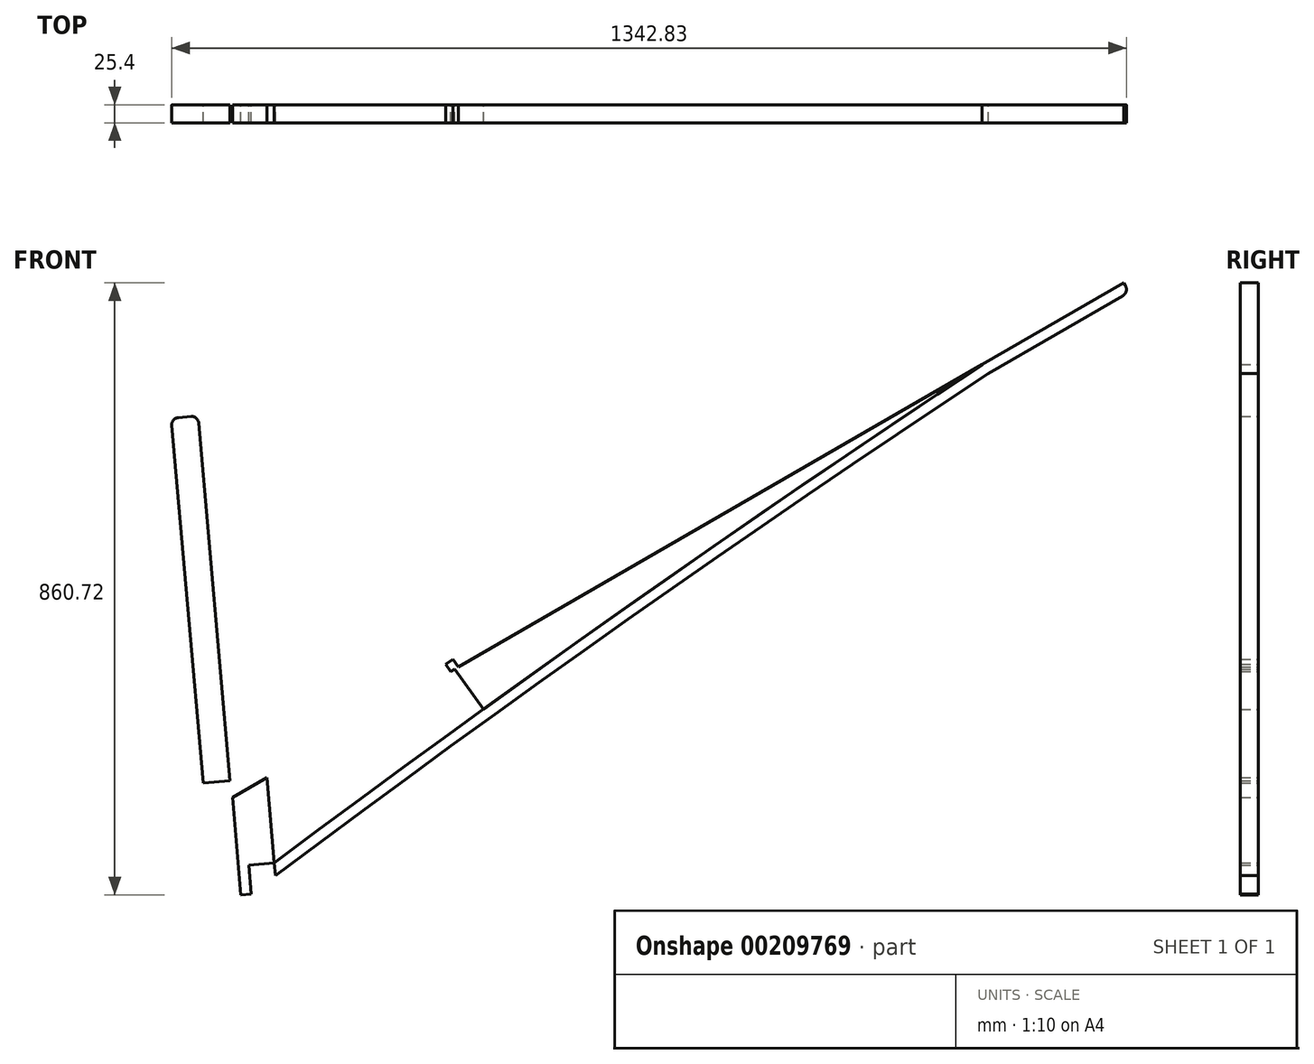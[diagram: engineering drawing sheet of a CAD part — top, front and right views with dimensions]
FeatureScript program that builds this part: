
annotation { "Feature Type Name" : "Feature", "Feature Type Description" : "" }
export const myFeature = defineFeature(function(context is Context, id is Id, definition is map)
    precondition{}
    {
        {
            var Q0;
            Q0=qCreatedBy(makeId("Front.planeOp"),FACE);
            var sketch = newSketch(context, id + "F0", { "sketchPlane" : qUnion([Q0])});
            skLineSegment(sketch, "E0", {"start": v(0.89, -10.12) * mm, "end": v(177.1, -2024.27) * mm});
            skLineSegment(sketch, "E1", {"start": v(0, 0) * mm, "end": v(2540, 0) * mm, "construction": true});
            skLineSegment(sketch, "E2", {"start": v(-279.2, -744.3) * mm, "end": v(1339.78, 190.41) * mm});
            skLineSegment(sketch, "E3", {"start": v(0, 0) * mm, "end": v(0, -2540) * mm, "construction": true});
            skLineSegment(sketch, "E4", {"start": v(62.95, -2024.27) * mm, "end": v(824.95, -2024.27) * mm});
            skLineSegment(sketch, "E5.0", {"start": v(38.84, -6.8) * mm, "end": v(215.35, -2024.27) * mm});
            skLineSegment(sketch, "E6", {"start": v(27.83, 2.44) * mm, "end": v(10.12, 0.89) * mm});
            skLineSegment(sketch, "E7", {"start": v(215.35, -2024.27) * mm, "end": v(177.1, -2024.27) * mm});
            skLineSegment(sketch, "E8.0", {"start": v(-298.26, -711.31) * mm, "end": v(1311.93, 218.33) * mm});
            skLineSegment(sketch, "E9", {"start": v(-293.08, -740.59) * mm, "end": v(-301.97, -725.2) * mm});
            skLineSegment(sketch, "E10", {"start": v(1339.78, 190.41) * mm, "end": v(1325.8, 214.6) * mm});
            skPoint(sketch, "E11", {"position": v(44.9, -513.2) * mm});
            skLineSegment(sketch, "E12", {"start": v(44.9, -513.2) * mm, "end": v(134.7, -505.33) * mm});
            skLineSegment(sketch, "E13", {"start": v(134.7, -505.33) * mm, "end": v(147.87, -655.76) * mm});
            skLineSegment(sketch, "E14", {"start": v(138.63, -666.77) * mm, "end": v(58.94, -673.74) * mm});
            skLineSegment(sketch, "E15", {"start": v(58.94, -673.74) * mm, "end": v(44.9, -513.2) * mm});
            skLineSegment(sketch, "E16", {"start": v(44.9, -513.2) * mm, "end": v(26.93, -514.76) * mm});
            skLineSegment(sketch, "E17", {"start": v(26.93, -514.76) * mm, "end": v(40.1, -665.2) * mm});
            skLineSegment(sketch, "E18", {"start": v(51.1, -674.43) * mm, "end": v(58.94, -673.74) * mm});
            skPoint(sketch, "E19", {"position": v(84.97, -534.05) * mm});
            skPoint(sketch, "E20", {"position": v(1140.83, 75.55) * mm});
            skLineSegment(sketch, "E21", {"start": v(147.18, -647.92) * mm, "end": v(39.4, -657.35) * mm, "construction": true});
            skCircle(sketch, "E22", {"center": v(129.22, -649.49) * mm, "radius": 8.26 * mm});
            skLineSegment(sketch, "E23", {"start": v(134.7, -505.33) * mm, "end": v(131.04, -463.46) * mm});
            skLineSegment(sketch, "E24", {"start": v(131.04, -463.46) * mm, "end": v(23.27, -472.89) * mm});
            skLineSegment(sketch, "E25", {"start": v(23.27, -472.89) * mm, "end": v(26.93, -514.76) * mm});
            skPoint(sketch, "E26", {"position": v(398.67, -352.93) * mm});
            skLineSegment(sketch, "E27", {"start": v(398.67, -352.93) * mm, "end": v(433.6, -413.43) * mm, "construction": true});
            skPoint(sketch, "E28", {"position": v(145.22, -625.53) * mm});
            skArc(sketch, "E29", {"start": v(1140.83, 75.55) * mm, "mid": v(637.9, -267.71) * mm, "end": v(145.22, -625.53) * mm});
            skArc(sketch, "E30.0", {"start": v(1149.23, 62.84) * mm, "mid": v(642.8, -282.9) * mm, "end": v(146.79, -643.4) * mm});
            skLineSegment(sketch, "E31", {"start": v(398.67, -352.93) * mm, "end": v(439.34, -409.28) * mm});
            skLineSegment(sketch, "E32.0", {"start": v(394.17, -357.54) * mm, "end": v(434.2, -413) * mm});
            skLineSegment(sketch, "E33.0", {"start": v(403.82, -349.22) * mm, "end": v(444.5, -405.56) * mm});
            skLineSegment(sketch, "E34", {"start": v(1339.78, 190.41) * mm, "end": v(1342.32, 186.01) * mm});
            skLineSegment(sketch, "E35", {"start": v(1149.23, 62.84) * mm, "end": v(1338.6, 172.13) * mm});
            skLineSegment(sketch, "E36.0", {"start": v(39.22, 3.43) * mm, "end": v(216.32, -2020.84) * mm, "construction": true});
            skLineSegment(sketch, "E37.0", {"start": v(-1.27, -0.11) * mm, "end": v(175.84, -2024.38) * mm, "construction": true});
            skLineSegment(sketch, "E38", {"start": v(39.97, -471.42) * mm, "end": v(57.67, -673.74) * mm});
            skLineSegment(sketch, "E39", {"start": v(80.45, -467.88) * mm, "end": v(98.16, -670.3) * mm});
            skLineSegment(sketch, "E40", {"start": v(145.22, -625.53) * mm, "end": v(109.3, -628.67) * mm});
            skLineSegment(sketch, "E41", {"start": v(109.3, -628.67) * mm, "end": v(112.82, -669.03) * mm});
            skPoint(sketch, "E42.visualSharp", {"position": v(148.75, -665.88) * mm});
            skArc(sketch, "E42.filletArc", {"start": v(138.63, -666.77) * mm, "mid": v(145.53, -663.18) * mm, "end": v(147.87, -655.76) * mm});
            skLineSegment(sketch, "E43", {"start": v(403.82, -349.22) * mm, "end": v(396.39, -338.92) * mm});
            skLineSegment(sketch, "E44", {"start": v(396.39, -338.92) * mm, "end": v(386.1, -346.35) * mm});
            skLineSegment(sketch, "E45", {"start": v(386.1, -346.35) * mm, "end": v(394.17, -357.54) * mm});
            skLineSegment(sketch, "E46", {"start": v(1140.83, 75.55) * mm, "end": v(1134.42, 86.65) * mm});
            skLineSegment(sketch, "E47", {"start": v(1134.42, 86.65) * mm, "end": v(1148.16, 94.59) * mm});
            skLineSegment(sketch, "E48", {"start": v(1148.16, 94.59) * mm, "end": v(1154.58, 83.49) * mm});
            skLineSegment(sketch, "E49", {"start": v(1326.03, 182.47) * mm, "end": v(1319.68, 193.47) * mm});
            skLineSegment(sketch, "E50", {"start": v(1319.68, 193.47) * mm, "end": v(1333.43, 201.41) * mm});
            skPoint(sketch, "E51.visualSharp", {"position": v(1347.4, 177.21) * mm});
            skArc(sketch, "E51.filletArc", {"start": v(1338.6, 172.13) * mm, "mid": v(1343.33, 178.3) * mm, "end": v(1342.32, 186.01) * mm});
            skPoint(sketch, "E52.visualSharp", {"position": v(1320.73, 223.4) * mm});
            skArc(sketch, "E52.filletArc", {"start": v(1325.8, 214.6) * mm, "mid": v(1319.64, 219.34) * mm, "end": v(1311.93, 218.33) * mm});
            skLineSegment(sketch, "E53.0", {"start": v(6.19, -484.58) * mm, "end": v(8.97, -516.34) * mm});
            skLineSegment(sketch, "E54", {"start": v(23.27, -472.89) * mm, "end": v(15.43, -473.57) * mm});
            skLineSegment(sketch, "E55", {"start": v(8.97, -516.34) * mm, "end": v(10.43, -533.1) * mm});
            skCircle(sketch, "E56", {"center": v(25.1, -491.17) * mm, "radius": 8.26 * mm});
            skPoint(sketch, "E57.visualSharp", {"position": v(5.3, -474.46) * mm});
            skArc(sketch, "E57.filletArc", {"start": v(15.43, -473.57) * mm, "mid": v(8.53, -477.16) * mm, "end": v(6.19, -484.58) * mm});
            skPoint(sketch, "E58.visualSharp", {"position": v(40.98, -675.31) * mm});
            skArc(sketch, "E58.filletArc", {"start": v(40.1, -665.2) * mm, "mid": v(43.68, -672.09) * mm, "end": v(51.1, -674.43) * mm});
            skPoint(sketch, "E59.visualSharp", {"position": v(37.96, 3.32) * mm});
            skArc(sketch, "E59.filletArc", {"start": v(38.84, -6.8) * mm, "mid": v(35.25, 0.1) * mm, "end": v(27.83, 2.44) * mm});
            skPoint(sketch, "E60.visualSharp", {"position": v(0, 0) * mm});
            skArc(sketch, "E60.filletArc", {"start": v(10.12, 0.89) * mm, "mid": v(3.22, -2.7) * mm, "end": v(0.89, -10.12) * mm});
            skPoint(sketch, "E61.visualSharp", {"position": v(-307.05, -716.4) * mm});
            skArc(sketch, "E61.filletArc", {"start": v(-298.26, -711.31) * mm, "mid": v(-302.99, -717.48) * mm, "end": v(-301.97, -725.2) * mm});
            skPoint(sketch, "E62.visualSharp", {"position": v(-288, -749.39) * mm});
            skArc(sketch, "E62.filletArc", {"start": v(-293.08, -740.59) * mm, "mid": v(-286.92, -745.32) * mm, "end": v(-279.2, -744.3) * mm});
            skLineSegment(sketch, "E63", {"start": v(147.12, -1771.92) * mm, "end": v(233.4, -1764.37) * mm});
            skLineSegment(sketch, "E64", {"start": v(244.41, -1773.6) * mm, "end": v(266.34, -2024.27) * mm});
            skLineSegment(sketch, "E65", {"start": v(137.88, -1782.93) * mm, "end": v(159, -2024.27) * mm});
            skPoint(sketch, "E66", {"position": v(192.92, -1767.91) * mm});
            skPoint(sketch, "E67", {"position": v(154.96, -1771.23) * mm});
            skLineSegment(sketch, "E68.0", {"start": v(62.95, -2042.3) * mm, "end": v(824.95, -2042.3) * mm});
            skLineSegment(sketch, "E69.0", {"start": v(73.1, -1988.2) * mm, "end": v(824.95, -1988.2) * mm});
            skLineSegment(sketch, "E70", {"start": v(62.95, -1998.36) * mm, "end": v(62.95, -2024.27) * mm});
            skLineSegment(sketch, "E71", {"start": v(62.95, -2042.3) * mm, "end": v(62.95, -2024.27) * mm});
            skLineSegment(sketch, "E72", {"start": v(824.95, -1988.2) * mm, "end": v(824.95, -2024.27) * mm});
            skLineSegment(sketch, "E73", {"start": v(824.95, -2024.27) * mm, "end": v(824.95, -2042.3) * mm});
            skLineSegment(sketch, "E74", {"start": v(774.15, -2024.27) * mm, "end": v(774.15, -2042.3) * mm});
            skLineSegment(sketch, "E75.bottom", {"start": v(266.34, -2024.27) * mm, "end": v(317.14, -2024.27) * mm});
            skLineSegment(sketch, "E75.top", {"start": v(266.34, -2042.3) * mm, "end": v(317.14, -2042.3) * mm});
            skLineSegment(sketch, "E75.left", {"start": v(266.34, -2024.27) * mm, "end": v(266.34, -2042.3) * mm});
            skLineSegment(sketch, "E75.right", {"start": v(317.14, -2024.27) * mm, "end": v(317.14, -2042.3) * mm});
            skLineSegment(sketch, "E76.bottom", {"start": v(62.95, -2024.27) * mm, "end": v(113.75, -2024.27) * mm});
            skLineSegment(sketch, "E76.top", {"start": v(62.95, -2042.3) * mm, "end": v(113.75, -2042.3) * mm});
            skLineSegment(sketch, "E76.left", {"start": v(62.95, -2024.27) * mm, "end": v(62.95, -2042.3) * mm});
            skLineSegment(sketch, "E76.right", {"start": v(113.75, -2024.27) * mm, "end": v(113.75, -2042.3) * mm});
            skPoint(sketch, "E77.visualSharp", {"position": v(62.95, -1988.2) * mm});
            skArc(sketch, "E77.filletArc", {"start": v(73.1, -1988.2) * mm, "mid": v(65.92, -1991.18) * mm, "end": v(62.95, -1998.36) * mm});
            skPoint(sketch, "E78.visualSharp", {"position": v(243.52, -1763.49) * mm});
            skArc(sketch, "E78.filletArc", {"start": v(244.41, -1773.6) * mm, "mid": v(240.82, -1766.7) * mm, "end": v(233.4, -1764.37) * mm});
            skPoint(sketch, "E79.visualSharp", {"position": v(137, -1772.8) * mm});
            skArc(sketch, "E79.filletArc", {"start": v(147.12, -1771.92) * mm, "mid": v(140.22, -1775.51) * mm, "end": v(137.88, -1782.93) * mm});
            skPoint(sketch, "E80", {"position": v(155.84, -1988.2) * mm});
            skLineSegment(sketch, "E81", {"start": v(155.84, -1988.2) * mm, "end": v(159, -2024.27) * mm});
            skCircle(sketch, "E82", {"center": v(157.42, -2006.23) * mm, "radius": 8.26 * mm});
            skLineSegment(sketch, "E83", {"start": v(195.78, -1786.02) * mm, "end": v(245.12, -1781.7) * mm, "construction": true});
            skCircle(sketch, "E84", {"center": v(220.45, -1783.86) * mm, "radius": 8.26 * mm});
            skPoint(sketch, "E84.perimeterSnap0", {"position": v(220.45, -1783.86) * mm});
            skPoint(sketch, "E84.perimeterSnap1", {"position": v(190.26, -1768.15) * mm});
            skLineSegment(sketch, "E85.bottom", {"start": v(73.1, -2194.7) * mm, "end": v(814.79, -2194.7) * mm});
            skLineSegment(sketch, "E85.top", {"start": v(73.1, -2499.5) * mm, "end": v(814.79, -2499.5) * mm});
            skLineSegment(sketch, "E85.left", {"start": v(62.95, -2204.86) * mm, "end": v(62.95, -2489.34) * mm});
            skLineSegment(sketch, "E85.right", {"start": v(824.95, -2204.86) * mm, "end": v(824.95, -2489.34) * mm});
            skLineSegment(sketch, "E86", {"start": v(62.95, -2347.1) * mm, "end": v(824.95, -2347.1) * mm, "construction": true});
            skLineSegment(sketch, "E87.0", {"start": v(62.95, -2365.14) * mm, "end": v(824.95, -2365.14) * mm, "construction": true});
            skLineSegment(sketch, "E88.0", {"start": v(62.95, -2329.07) * mm, "end": v(824.95, -2329.07) * mm, "construction": true});
            skLineSegment(sketch, "E89.bottom", {"start": v(266.34, -2329.07) * mm, "end": v(317.14, -2329.07) * mm});
            skLineSegment(sketch, "E89.top", {"start": v(266.34, -2311.03) * mm, "end": v(317.14, -2311.03) * mm});
            skLineSegment(sketch, "E89.left", {"start": v(266.34, -2329.07) * mm, "end": v(266.34, -2311.03) * mm});
            skLineSegment(sketch, "E89.right", {"start": v(317.14, -2329.07) * mm, "end": v(317.14, -2311.03) * mm});
            skLineSegment(sketch, "E90.bottom", {"start": v(774.15, -2329.07) * mm, "end": v(824.95, -2329.07) * mm});
            skLineSegment(sketch, "E90.top", {"start": v(774.15, -2311.03) * mm, "end": v(824.95, -2311.03) * mm});
            skLineSegment(sketch, "E90.left", {"start": v(774.15, -2329.07) * mm, "end": v(774.15, -2311.03) * mm});
            skLineSegment(sketch, "E90.right", {"start": v(824.95, -2329.07) * mm, "end": v(824.95, -2311.03) * mm});
            skLineSegment(sketch, "E91.bottom", {"start": v(62.95, -2311.03) * mm, "end": v(113.75, -2311.03) * mm});
            skLineSegment(sketch, "E91.top", {"start": v(62.95, -2329.07) * mm, "end": v(113.75, -2329.07) * mm});
            skLineSegment(sketch, "E91.left", {"start": v(62.95, -2311.03) * mm, "end": v(62.95, -2329.07) * mm});
            skLineSegment(sketch, "E91.right", {"start": v(113.75, -2311.03) * mm, "end": v(113.75, -2329.07) * mm});
            skLineSegment(sketch, "E92.MirrorCS", {"start": v(62.95, -2365.14) * mm, "end": v(113.75, -2365.14) * mm});
            skLineSegment(sketch, "E93.MirrorCS", {"start": v(266.34, -2365.14) * mm, "end": v(317.14, -2365.14) * mm});
            skLineSegment(sketch, "E94.MirrorCS", {"start": v(774.15, -2365.14) * mm, "end": v(824.95, -2365.14) * mm});
            skLineSegment(sketch, "E95.MirrorCS", {"start": v(62.95, -2383.17) * mm, "end": v(113.75, -2383.17) * mm});
            skLineSegment(sketch, "E96.MirrorCS", {"start": v(824.95, -2365.14) * mm, "end": v(824.95, -2383.17) * mm});
            skLineSegment(sketch, "E97.MirrorCS", {"start": v(266.34, -2383.17) * mm, "end": v(317.14, -2383.17) * mm});
            skLineSegment(sketch, "E98.MirrorCS", {"start": v(774.15, -2365.14) * mm, "end": v(774.15, -2383.17) * mm});
            skLineSegment(sketch, "E99.MirrorCS", {"start": v(317.14, -2365.14) * mm, "end": v(317.14, -2383.17) * mm});
            skLineSegment(sketch, "E100.MirrorCS", {"start": v(266.34, -2365.14) * mm, "end": v(266.34, -2383.17) * mm});
            skLineSegment(sketch, "E101.MirrorCS", {"start": v(62.95, -2383.17) * mm, "end": v(62.95, -2365.14) * mm});
            skLineSegment(sketch, "E102.MirrorCS", {"start": v(113.75, -2383.17) * mm, "end": v(113.75, -2365.14) * mm});
            skLineSegment(sketch, "E103.MirrorCS", {"start": v(774.15, -2383.17) * mm, "end": v(824.95, -2383.17) * mm});
            skPoint(sketch, "E104.visualSharp", {"position": v(62.95, -2194.7) * mm});
            skArc(sketch, "E104.filletArc", {"start": v(73.1, -2194.7) * mm, "mid": v(65.92, -2197.68) * mm, "end": v(62.95, -2204.86) * mm});
            skPoint(sketch, "E105.visualSharp", {"position": v(824.95, -2194.7) * mm});
            skArc(sketch, "E105.filletArc", {"start": v(824.95, -2204.86) * mm, "mid": v(821.97, -2197.68) * mm, "end": v(814.79, -2194.7) * mm});
            skPoint(sketch, "E106.visualSharp", {"position": v(824.95, -2499.5) * mm});
            skArc(sketch, "E106.filletArc", {"start": v(814.79, -2499.5) * mm, "mid": v(821.97, -2496.53) * mm, "end": v(824.95, -2489.34) * mm});
            skPoint(sketch, "E107.visualSharp", {"position": v(62.95, -2499.5) * mm});
            skArc(sketch, "E107.filletArc", {"start": v(62.95, -2489.34) * mm, "mid": v(65.92, -2496.53) * mm, "end": v(73.1, -2499.5) * mm});
            skPoint(sketch, "E108", {"position": v(81.3, -492.17) * mm});
            skLineSegment(sketch, "E109", {"start": v(131.04, -463.46) * mm, "end": v(84.97, -534.05) * mm, "construction": true});
            skLineSegment(sketch, "E110", {"start": v(81.3, -492.17) * mm, "end": v(134.7, -505.33) * mm, "construction": true});
            skCircle(sketch, "E111", {"center": v(108, -498.75) * mm, "radius": 8.26 * mm});
            skLineSegment(sketch, "E112", {"start": v(1267.05, 192.42) * mm, "end": v(1273.4, 181.42) * mm});
            skLineSegment(sketch, "E113", {"start": v(1273.4, 181.42) * mm, "end": v(1283.08, 187) * mm});
            skLineSegment(sketch, "E114", {"start": v(1283.08, 187) * mm, "end": v(1276.73, 198) * mm});
            skCircle(sketch, "E115", {"center": v(1271.18, 185.27) * mm, "radius": 4.45 * mm});
            skLineSegment(sketch, "E116", {"start": v(1169.39, 136.03) * mm, "end": v(1175.74, 125.03) * mm});
            skLineSegment(sketch, "E117", {"start": v(1175.74, 125.03) * mm, "end": v(1185.42, 130.62) * mm});
            skLineSegment(sketch, "E118", {"start": v(1185.42, 130.62) * mm, "end": v(1179.07, 141.62) * mm});
            skCircle(sketch, "E119", {"center": v(1173.51, 128.88) * mm, "radius": 4.45 * mm});
            skLineSegment(sketch, "E120", {"start": v(1179.07, 141.62) * mm, "end": v(1169.39, 136.03) * mm});
            skLineSegment(sketch, "E121", {"start": v(1071.72, 79.64) * mm, "end": v(1078.07, 68.65) * mm});
            skLineSegment(sketch, "E122", {"start": v(1078.07, 68.65) * mm, "end": v(1087.75, 74.23) * mm});
            skLineSegment(sketch, "E123", {"start": v(1087.75, 74.23) * mm, "end": v(1081.4, 85.23) * mm});
            skCircle(sketch, "E124", {"center": v(1075.85, 72.5) * mm, "radius": 4.45 * mm});
            skLineSegment(sketch, "E125", {"start": v(1081.4, 85.23) * mm, "end": v(1071.72, 79.64) * mm});
            skLineSegment(sketch, "E126", {"start": v(974.05, 23.26) * mm, "end": v(980.4, 12.26) * mm});
            skLineSegment(sketch, "E127", {"start": v(980.4, 12.26) * mm, "end": v(990.08, 17.85) * mm});
            skLineSegment(sketch, "E128", {"start": v(990.08, 17.85) * mm, "end": v(983.73, 28.84) * mm});
            skCircle(sketch, "E129", {"center": v(978.18, 16.1) * mm, "radius": 4.45 * mm});
            skLineSegment(sketch, "E130", {"start": v(983.73, 28.84) * mm, "end": v(974.05, 23.26) * mm});
            skLineSegment(sketch, "E131", {"start": v(876.39, -33.13) * mm, "end": v(882.74, -44.13) * mm});
            skLineSegment(sketch, "E132", {"start": v(882.74, -44.13) * mm, "end": v(892.42, -38.54) * mm});
            skLineSegment(sketch, "E133", {"start": v(892.42, -38.54) * mm, "end": v(886.07, -27.54) * mm});
            skCircle(sketch, "E134", {"center": v(880.51, -40.28) * mm, "radius": 4.45 * mm});
            skLineSegment(sketch, "E135", {"start": v(886.07, -27.54) * mm, "end": v(876.39, -33.13) * mm});
            skLineSegment(sketch, "E136", {"start": v(778.72, -89.52) * mm, "end": v(785.07, -100.52) * mm});
            skLineSegment(sketch, "E137", {"start": v(785.07, -100.52) * mm, "end": v(794.75, -94.93) * mm});
            skLineSegment(sketch, "E138", {"start": v(794.75, -94.93) * mm, "end": v(788.4, -83.93) * mm});
            skCircle(sketch, "E139", {"center": v(782.85, -96.67) * mm, "radius": 4.45 * mm});
            skLineSegment(sketch, "E140", {"start": v(788.4, -83.93) * mm, "end": v(778.72, -89.52) * mm});
            skLineSegment(sketch, "E141", {"start": v(263.18, -1988.2) * mm, "end": v(824.95, -2006.23) * mm});
            skSolve(sketch);
        }
        {
            var Q0;
            Q0=makeQuery(id+"F0.imprint","IMPRINT",FACE,{"disambiguationData":[TD([[makeQuery(id+"F0.imprint","IMPRINT",EDGE,{"derivedFrom":sQuery(id+"F0.wireOp",EDGE,"E6")}),1.0]])]});
            var Q1;
            {var subQ3=sQuery(id+"F0.wireOp",EDGE,"E24");var subQ5=sQuery(id+"F0.wireOp",EDGE,"E5.0");var subQ6=makeQuery(id+"F0.imprint","INTERSECT",VERTEX,{"derivedFrom":[subQ5,subQ3]});Q1=makeQuery(id+"F0.imprint","IMPRINT",FACE,{"disambiguationData":[TD([[makeQuery(id+"F0.imprint","IMPRINT",EDGE,{"disambiguationData":[TD([[subQ6,-1.0]])],"derivedFrom":subQ5}),-1.0]])]});}
            var Q2;
            {var subQ0=sQuery(id+"F0.wireOp",EDGE,"E8.0");var subQ1=sQuery(id+"F0.wireOp",EDGE,"E5.0");var subQ2=makeQuery(id+"F0.imprint","INTERSECT",VERTEX,{"derivedFrom":[subQ1,subQ0]});Q2=makeQuery(id+"F0.imprint","IMPRINT",FACE,{"disambiguationData":[TD([[makeQuery(id+"F0.imprint","IMPRINT",EDGE,{"disambiguationData":[TD([[subQ2,-1.0]])],"derivedFrom":subQ1}),-1.0]])]});}
            var Q3;
            {var subQ0=sQuery(id+"F0.wireOp",EDGE,"E15");var subQ1=sQuery(id+"F0.wireOp",EDGE,"E2");var subQ2=makeQuery(id+"F0.imprint","INTERSECT",VERTEX,{"derivedFrom":[subQ1,subQ0]});Q3=makeQuery(id+"F0.imprint","IMPRINT",FACE,{"disambiguationData":[TD([[makeQuery(id+"F0.imprint","IMPRINT",EDGE,{"disambiguationData":[TD([[subQ2,-1.0]])],"derivedFrom":subQ1}),1.0]])]});}
            var Q4;
            {var subQ8=sQuery(id+"F0.wireOp",EDGE,"E40");Q4=makeQuery(id+"F0.imprint","IMPRINT",FACE,{"disambiguationData":[TD([[makeQuery(id+"F0.imprint","IMPRINT",EDGE,{"derivedFrom":subQ8}),-1.0]])]});}
            var Q5;
            {var subQ0=sQuery(id+"F0.wireOp",EDGE,"E15");var subQ1=sQuery(id+"F0.wireOp",EDGE,"E2");var subQ2=makeQuery(id+"F0.imprint","INTERSECT",VERTEX,{"derivedFrom":[subQ1,subQ0]});Q5=makeQuery(id+"F0.imprint","IMPRINT",FACE,{"disambiguationData":[TD([[makeQuery(id+"F0.imprint","IMPRINT",EDGE,{"disambiguationData":[TD([[subQ2,-1.0]])],"derivedFrom":subQ1}),-1.0]])]});}
            extrude(context, id + "F1", {"entities" : qUnion([Q0, Q1, Q2, Q3, Q4, Q5]), "depth" : 25.4 * mm});
        }
        {
            var Q0;
            {var subQ3=sQuery(id+"F0.wireOp",EDGE,"E30.0");Q0=makeQuery(id+"F0.imprint","IMPRINT",FACE,{"disambiguationData":[TD([[makeQuery(id+"F0.imprint","IMPRINT",EDGE,{"derivedFrom":subQ3}),-1.0]])]});}
            extrude(context, id + "F2", {"entities" : qUnion([Q0]), "depth" : 25.4 * mm});
        }
    });
